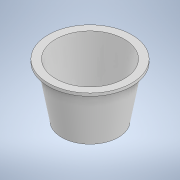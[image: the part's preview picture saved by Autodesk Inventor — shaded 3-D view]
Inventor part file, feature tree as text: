
AUTODESK INVENTOR PART (.ipt)
format: ipt  version: 2020 (Build 240168000, 168)  size: 122,368 bytes
history: native  units: mm
features: revolve x1, sketch x1
ambient origin geometry x8: Origin, YZ Plane, XZ Plane, XY Plane, X Axis, Y Axis, Z Axis, Center Point
bodies: Solid1 (feature_tree)
feature tree (2):
  revolve  "Revolution1"  [1 undecoded]
  sketch  "Sketch1"  dims[d0=2.5mm d1=22.0mm d2=45.0mm d3=1.745329mm d4=6.5mm d5=2.5mm d6=90.0deg]
note: 1 required parameter value undecoded (feature->parameter linkage not recoverable at this tier; creation-order binding heuristic only, values carry confidence <= 0.55)
